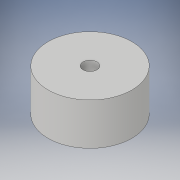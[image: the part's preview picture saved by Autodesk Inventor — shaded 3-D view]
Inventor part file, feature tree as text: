
AUTODESK INVENTOR PART (.ipt)
format: ipt  version: 2019 (Build 230136000, 136)  size: 96,768 bytes
history: native  units: mm
features: extrude x1, sketch x1
ambient origin geometry x8: Origin, YZ Plane, XZ Plane, XY Plane, X Axis, Y Axis, Z Axis, Center Point
bodies: Solid1 (feature_tree)
feature tree (2):
  extrude  "Extrusion1"  Depth=15.0mm
  sketch  "Sketch1"  dims[d0=30.0mm d1=5.0mm d2=15.0mm d3=0.0mm]
